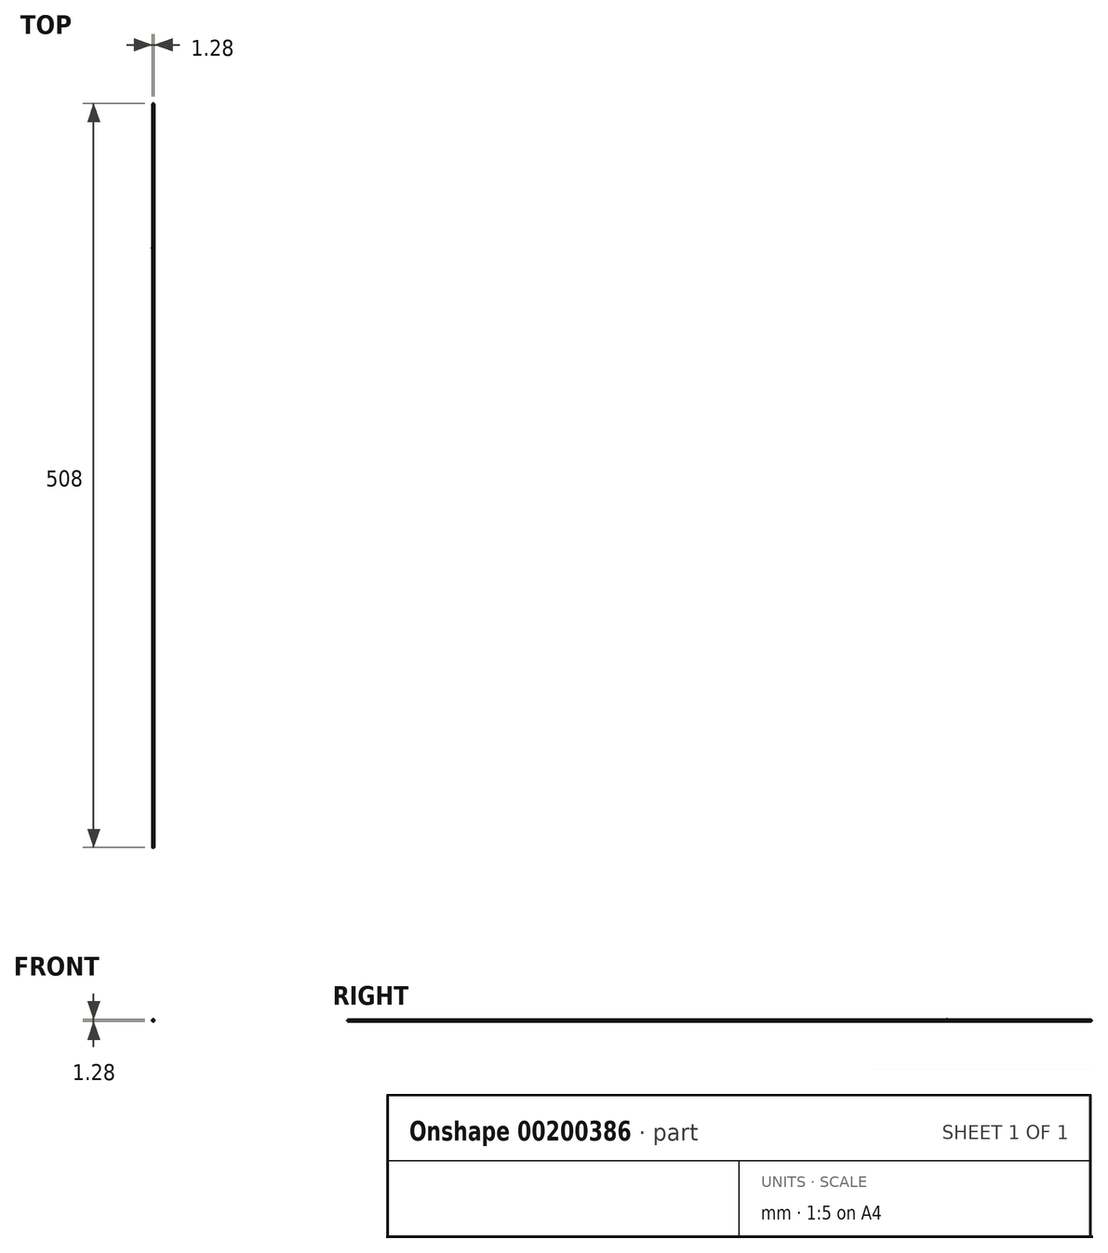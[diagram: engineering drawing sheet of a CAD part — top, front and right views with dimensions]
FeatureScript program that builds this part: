
annotation { "Feature Type Name" : "Feature", "Feature Type Description" : "" }
export const myFeature = defineFeature(function(context is Context, id is Id, definition is map)
    precondition{}
    {
        {
            var Q0;
            Q0=qCreatedBy(makeId("Front.planeOp"),FACE);
            var sketch = newSketch(context, id + "F0", { "sketchPlane" : qUnion([Q0])});
            skCircle(sketch, "E0", {"center": v(0, 0) * mm, "radius": 0.44 * mm});
            skSolve(sketch);
        }
        {
            var Q0;
            Q0 = qSketchRegion(id + "F0", true);
            extrude(context, id + "F1", {"entities" : qUnion([Q0]), "depth" : 508 * mm});
        }
        {
            var Q0;
            Q0=qCreatedBy(makeId("Front.planeOp"),FACE);
            cPlane(context, id + "F2", {"entities" : qUnion([Q0]), "cplaneType" : CPlaneType.OFFSET, "offset" : 99.82 * mm, "width" : 152.4 * mm, "height" : 152.4 * mm});
        }
        {
            var Q0;
            Q0=qCreatedBy(id+"F2.planeOp",FACE);
            var sketch = newSketch(context, id + "F3", { "sketchPlane" : qUnion([Q0])});
            skCircle(sketch, "E1", {"center": v(0, 0) * mm, "radius": 0.64 * mm});
            skSolve(sketch);
        }
        {
            var Q0;
            Q0 = qSketchRegion(id + "F3", true);
            extrude(context, id + "F4", {"entities" : qUnion([Q0]), "operationType" : NewBodyOperationType.ADD, "oppositeDirection" : true, "depth" : 2.54 * mm});
        }
        {
            var Q0;
            Q0=makeQuery(id+"F4.opExtrude","CAP_EDGE",EDGE,{"disambiguationData":[OSD([sQuery(id+"F3.wireOp",EDGE,"E1")])],"isStart":false});
            chamfer(context, id + "F5", {"entities" : qUnion([Q0]), "chamferType" : ChamferType.TWO_OFFSETS, "width1" : 1.02 * mm, "oppositeDirection" : false, "width2" : 0.5 * mm, "tangentPropagation" : true});
        }
        {
            var Q0;
            Q0=makeQuery(id+"F4.opExtrude","CAP_EDGE",EDGE,{"disambiguationData":[OSD([sQuery(id+"F3.wireOp",EDGE,"E1")])],"isStart":true});
            chamfer(context, id + "F6", {"entities" : qUnion([Q0]), "chamferType" : ChamferType.TWO_OFFSETS, "width1" : 0.5 * mm, "oppositeDirection" : false, "width2" : 1.02 * mm, "tangentPropagation" : true});
        }
        {
            var Q0;
            Q0=makeQuery(id+"F1.opExtrude","CAP_EDGE",EDGE,{"disambiguationData":[OSD([sQuery(id+"F0.wireOp",EDGE,"E0")])],"isStart":true});
            fillet(context, id + "F7", {"entities" : qUnion([Q0]), "radius" : 0.42 * mm, "tangentPropagation" : true, "allowEdgeOverflow" : false});
        }
    });
